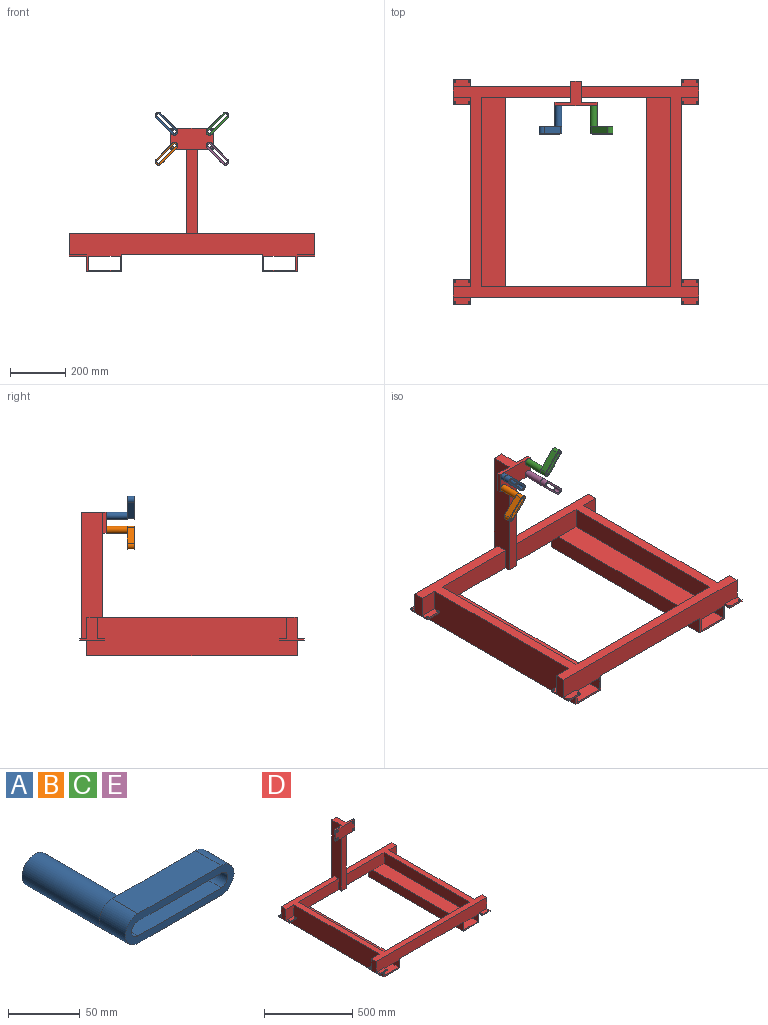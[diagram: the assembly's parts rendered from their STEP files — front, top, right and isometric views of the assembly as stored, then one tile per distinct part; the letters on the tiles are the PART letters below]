
ASSEMBLY  parts=5 mates=4
PART A: 14 faces, bbox 107.4x101.6x25.4 mm
  f0: plane 12.7x12.7mm, normal (0,-1,0), area 91mm2, adj f1,f2,f9,f11
  f1: cylinder r=6.35mm len=101.6mm, axis (0,-1,0), area 3547mm2, adj f0,f3,f9,f11,f13
  f2: cylinder r=12.7mm len=76.2mm, axis (0,-1,0), area 6080.5mm2, adj f0,f3,f4,f5
  f3: plane 25.4x25.4mm, normal (0,1,0), area 380mm2, adj f1,f2
  f4: plane 25.4x14.3mm, normal (0,-1,0), area 4.3mm2, adj f2,f6,f7,f8
  f5: plane 93.05x25.2mm, normal (0,1,0), area 1112.5mm2, adj f2,f6,f8,f9,f10,f11,f12
  f6: plane 82.05x25.4mm, normal (0,0,1), area 2084.1mm2, adj f4,f5,f7,f12,f13
  f7: cylinder r=12.6mm len=25.4mm, axis (0,1,0), area 1005.3mm2, adj f4,f6,f8,f13
  f8: plane 82.05x25.4mm, normal (0,0,-1), area 2084.1mm2, adj f4,f5,f7,f12,f13
  f9: plane 82.05x25.4mm, normal (0,0,-1), area 2084.1mm2, adj f0,f1,f5,f10,f13
  f10: cylinder r=6.35mm len=25.4mm, axis (0,1,0), area 506.7mm2, adj f5,f9,f11,f13
  f11: plane 82.05x25.4mm, normal (0,0,1), area 2084.1mm2, adj f0,f1,f5,f10,f13
  f12: cylinder r=12.6mm len=25.4mm, axis (0,1,0), area 1005.3mm2, adj f5,f6,f8,f13
  f13: plane 107.25x25.2mm, normal (0,-1,0), area 1397.3mm2, adj f1,f6,f7,f8,f9,f10,f11,f12
PART B: same geometry as A
PART C: same geometry as A
PART D: 94 faces, bbox 889x812.8x520.7 mm
  f0: plane 381x38.1mm, normal (0,-1,0), area 14516.1mm2, adj f6,f80,f81,f88
  f1: plane 425.45x139.7mm, normal (0,1,0), area 34677.3mm2, adj f3,f6,f9,f19,f25,f56,f70,f71
  f2: plane 323.85x76.2mm, normal (0,-1,0), area 24677.4mm2, adj f3,f6,f23,f69,f80
  f3: plane 889x762mm, normal (0,0,1), area 118548.2mm2, adj f1,f2,f10,f11,f12,f13,f14,f15
  f4: plane 38.1x1.27mm, normal (0,0,-1), area 48.4mm2, adj f16,f18,f19,f39
  f5: plane 508x38.1mm, normal (0,0,-1), area 19354.8mm2, adj f16,f24,f67,f70
  f6: plane 508x76.2mm, normal (0,0,-1), area 20806.4mm2, adj f0,f1,f2,f10,f22,f67,f70,f80
  f7: plane 38.1x1.27mm, normal (0,0,-1), area 48.4mm2, adj f10,f12,f13,f48
  f8: plane 38.1x1.27mm, normal (0,0,-1), area 48.4mm2, adj f13,f14,f16,f29
  f9: plane 38.1x1.27mm, normal (0,0,-1), area 48.4mm2, adj f1,f19,f20,f60
  f10: plane 425.45x139.7mm, normal (0,1,0), area 34677.4mm2, adj f3,f6,f7,f11,f13,f55,f67,f68
  f11: plane 88.9x82.55mm, normal (-1,0,0), area 3467.7mm2, adj f3,f10,f12,f46,f47,f50,f54,f55
  f12: plane 76.2x63.5mm, normal (0,-1,0), area 4838.7mm2, adj f3,f7,f11,f13,f46
  f13: plane 762x139.7mm, normal (-1,0,0), area 100645mm2, adj f3,f7,f8,f10,f12,f14,f16,f68
  f14: plane 76.2x63.5mm, normal (0,1,0), area 4838.7mm2, adj f3,f8,f13,f15,f27
  f15: plane 88.9x82.55mm, normal (-1,0,0), area 3467.7mm2, adj f3,f14,f16,f26,f27,f28,f30,f35
  f16: plane 889x139.7mm, normal (0,-1,0), area 72257.9mm2, adj f3,f4,f5,f8,f13,f15,f17,f19
  f17: plane 88.9x82.55mm, normal (1,0,0), area 3467.7mm2, adj f3,f16,f18,f36,f37,f38,f43,f45
  f18: plane 76.2x63.5mm, normal (0,1,0), area 4838.7mm2, adj f3,f4,f17,f19,f37
  f19: plane 762x139.7mm, normal (1,0,0), area 100645mm2, adj f1,f3,f4,f9,f16,f18,f20,f71
  f20: plane 76.2x63.5mm, normal (0,-1,0), area 4838.7mm2, adj f3,f9,f19,f25,f65
  f21: plane 685.8x76.2mm, normal (1,0,0), area 52258mm2, adj f3,f22,f24,f66
  f22: plane 323.85x76.2mm, normal (0,-1,0), area 24677.4mm2, adj f3,f6,f21,f66,f81
  f23: plane 685.8x76.2mm, normal (-1,0,0), area 52258mm2, adj f2,f3,f24,f69
  f24: plane 685.8x76.2mm, normal (0,1,0), area 52258mm2, adj f3,f5,f21,f23,f66,f69
  f25: plane 88.9x82.55mm, normal (1,0,0), area 3467.7mm2, adj f1,f3,f20,f56,f57,f58,f64,f65
  f26: plane 62.23x25.4mm, normal (0,0,1), area 1517.3mm2, adj f15,f16,f29,f30,f32,f33
  f27: plane 62.23x25.4mm, normal (0,0,1), area 1517.3mm2, adj f14,f15,f28,f29,f31,f34
  f28: plane 62.23x6.35mm, normal (0,1,0), area 395.2mm2, adj f15,f27,f29,f35
  f29: plane 88.9x6.35mm, normal (1,0,0), area 564.5mm2, adj f8,f26,f27,f28,f30,f35
  f30: plane 62.23x6.35mm, normal (0,-1,0), area 395.2mm2, adj f15,f26,f29,f35
  f31: cylinder r=3.17mm len=6.35mm, axis (0,0,1), area 126.7mm2, adj f27,f35
  f32: cylinder r=3.17mm len=6.35mm, axis (0,0,1), area 126.7mm2, adj f26,f35
  f33: cylinder r=3.17mm len=6.35mm, axis (0,0,1), area 126.7mm2, adj f26,f35
  f34: cylinder r=3.17mm len=6.35mm, axis (0,0,1), area 126.7mm2, adj f27,f35
  f35: plane 88.9x62.23mm, normal (0,0,-1), area 5405.6mm2, adj f15,f28,f29,f30,f31,f32,f33,f34
  f36: plane 62.23x25.4mm, normal (0,0,1), area 1517.3mm2, adj f16,f17,f38,f39,f41,f42
  f37: plane 62.23x25.4mm, normal (0,0,1), area 1517.3mm2, adj f17,f18,f39,f40,f43,f44
  f38: plane 62.23x6.35mm, normal (0,-1,0), area 395.2mm2, adj f17,f36,f39,f45
  f39: plane 88.9x6.35mm, normal (-1,0,0), area 564.5mm2, adj f4,f36,f37,f38,f43,f45
  f40: cylinder r=3.17mm len=6.35mm, axis (0,0,1), area 126.7mm2, adj f37,f45
  f41: cylinder r=3.17mm len=6.35mm, axis (0,0,1), area 126.7mm2, adj f36,f45
  f42: cylinder r=3.17mm len=6.35mm, axis (0,0,1), area 126.7mm2, adj f36,f45
  f43: plane 62.23x6.35mm, normal (0,1,0), area 395.2mm2, adj f17,f37,f39,f45
  f44: cylinder r=3.17mm len=6.35mm, axis (0,0,1), area 126.7mm2, adj f37,f45
  f45: plane 88.9x62.23mm, normal (0,0,-1), area 5405.6mm2, adj f17,f38,f39,f40,f41,f42,f43,f44
  f46: plane 62.23x25.4mm, normal (0,0,1), area 1517.3mm2, adj f11,f12,f48,f50,f51,f52
  f47: plane 62.23x6.35mm, normal (0,1,0), area 395.2mm2, adj f11,f48,f54,f55
  f48: plane 88.9x6.35mm, normal (1,0,0), area 564.5mm2, adj f7,f46,f47,f50,f54,f55
  f49: cylinder r=3.17mm len=6.35mm, axis (0,0,1), area 126.7mm2, adj f54,f55
  f50: plane 62.23x6.35mm, normal (0,-1,0), area 395.2mm2, adj f11,f46,f48,f54
  f51: cylinder r=3.17mm len=6.35mm, axis (0,0,1), area 126.7mm2, adj f46,f54
  f52: cylinder r=3.17mm len=6.35mm, axis (0,0,1), area 126.7mm2, adj f46,f54
  f53: cylinder r=3.17mm len=6.35mm, axis (0,0,1), area 126.7mm2, adj f54,f55
  f54: plane 88.9x62.23mm, normal (0,0,-1), area 5405.6mm2, adj f11,f47,f48,f49,f50,f51,f52,f53
  f55: plane 62.23x25.4mm, normal (0,0,1), area 1517.3mm2, adj f10,f11,f47,f48,f49,f53
  f56: plane 62.23x25.4mm, normal (0,0,1), area 1517.3mm2, adj f1,f25,f57,f60,f61,f62
  f57: plane 62.23x6.35mm, normal (0,1,0), area 395.2mm2, adj f25,f56,f60,f64
  f58: plane 62.23x6.35mm, normal (0,-1,0), area 395.2mm2, adj f25,f60,f64,f65
  f59: cylinder r=3.17mm len=6.35mm, axis (0,0,1), area 126.7mm2, adj f64,f65
  f60: plane 88.9x6.35mm, normal (-1,0,0), area 564.5mm2, adj f9,f56,f57,f58,f64,f65
  f61: cylinder r=3.17mm len=6.35mm, axis (0,0,1), area 126.7mm2, adj f56,f64
  f62: cylinder r=3.17mm len=6.35mm, axis (0,0,1), area 126.7mm2, adj f56,f64
  f63: cylinder r=3.17mm len=6.35mm, axis (0,0,1), area 126.7mm2, adj f64,f65
  f64: plane 88.9x62.23mm, normal (0,0,-1), area 5405.6mm2, adj f25,f57,f58,f59,f60,f61,f62,f63
  f65: plane 62.23x25.4mm, normal (0,0,1), area 1517.3mm2, adj f20,f25,f58,f59,f60,f63
  f66: plane 685.8x88.9mm, normal (0,0,1), area 60967.6mm2, adj f21,f22,f24,f67
  f67: plane 762x63.5mm, normal (1,0,0), area 48387mm2, adj f5,f6,f10,f16,f66,f68
  f68: plane 762x127mm, normal (0,0,-1), area 96774mm2, adj f10,f13,f16,f67
  f69: plane 685.8x88.9mm, normal (0,0,1), area 60967.6mm2, adj f2,f23,f24,f70
  f70: plane 762x63.5mm, normal (-1,0,0), area 48387mm2, adj f1,f5,f6,f16,f69,f71
  f71: plane 762x127mm, normal (0,0,-1), area 96774mm2, adj f1,f16,f19,f70
  f72: plane 762x114.3mm, normal (0,0,1), area 87096.6mm2, adj f1,f16,f73,f74
  f73: plane 762x50.8mm, normal (1,0,0), area 38709.6mm2, adj f1,f16,f72,f75
  f74: plane 762x50.8mm, normal (-1,0,0), area 38709.6mm2, adj f1,f16,f72,f75
  f75: plane 762x114.3mm, normal (0,0,-1), area 87096.6mm2, adj f1,f16,f73,f74
  f76: plane 762x50.8mm, normal (-1,0,0), area 38709.6mm2, adj f10,f16,f77,f78
  f77: plane 762x114.3mm, normal (0,0,1), area 87096.6mm2, adj f10,f16,f76,f79
  f78: plane 762x114.3mm, normal (0,0,-1), area 87096.6mm2, adj f10,f16,f76,f79
  f79: plane 762x50.8mm, normal (1,0,0), area 38709.6mm2, adj f10,f16,f77,f78
  f80: plane 457.2x76.2mm, normal (1,0,0), area 31935.4mm2, adj f0,f1,f2,f3,f6,f82,f83,f93
  f81: plane 457.2x76.2mm, normal (-1,0,0), area 31935.4mm2, adj f0,f3,f6,f10,f22,f82,f83,f84
  f82: plane 457.2x38.1mm, normal (0,1,0), area 17419.3mm2, adj f6,f80,f81,f83
  f83: plane 152.4x88.9mm, normal (0,0,1), area 4838.7mm2, adj f80,f81,f82,f84,f85,f86,f92,f93
  f84: plane 76.2x57.15mm, normal (0,1,0), area 4101.5mm2, adj f81,f83,f86,f87,f88,f91
  f85: plane 76.2x12.7mm, normal (1,0,0), area 967.7mm2, adj f83,f88,f92,f93
  f86: plane 76.2x12.7mm, normal (-1,0,0), area 967.7mm2, adj f83,f84,f88,f92
  f87: cylinder r=6.35mm len=12.7mm, axis (0,1,0), area 506.7mm2, adj f84,f92
  f88: plane 152.4x12.7mm, normal (0,0,-1), area 1935.5mm2, adj f0,f84,f85,f86,f92,f93
  f89: cylinder r=6.35mm len=12.7mm, axis (0,1,0), area 506.7mm2, adj f92,f93
  f90: cylinder r=6.35mm len=12.7mm, axis (0,1,0), area 506.7mm2, adj f92,f93
  f91: cylinder r=6.35mm len=12.7mm, axis (0,1,0), area 506.7mm2, adj f84,f92
  f92: plane 152.4x76.2mm, normal (0,-1,0), area 11106.2mm2, adj f83,f85,f86,f87,f88,f89,f90,f91
  f93: plane 76.2x57.15mm, normal (0,1,0), area 4101.5mm2, adj f80,f83,f85,f88,f89,f90
PART E: same geometry as A
PLACE A rot(axis=(0,-1,0),135deg) t=(-899.36,-6.49,563.89)mm
PLACE B rot(axis=(0,1,0),135deg) t=(-899.36,-6.49,513.09)mm
PLACE C rot(axis=(0,-1,0),45deg) t=(-772.36,-6.49,563.89)mm
PLACE D t=(-835.86,-241.44,119.39)mm
PLACE E rot(axis=(0,1,0),45deg) t=(-772.36,-6.49,513.09)mm
MATE revolute D.f90 <-> E.f2  axis (0,-1,0) through (-772.36,69.71,513.09)mm
MATE revolute D.f91 <-> A.f1  axis (0,1,0) through (-899.36,69.71,563.89)mm
MATE revolute D.f89 <-> C.f1  axis (0,-1,0) through (-772.36,69.71,563.89)mm
MATE revolute D.f87 <-> B.f1  axis (0,-1,0) through (-899.36,69.71,513.09)mm
